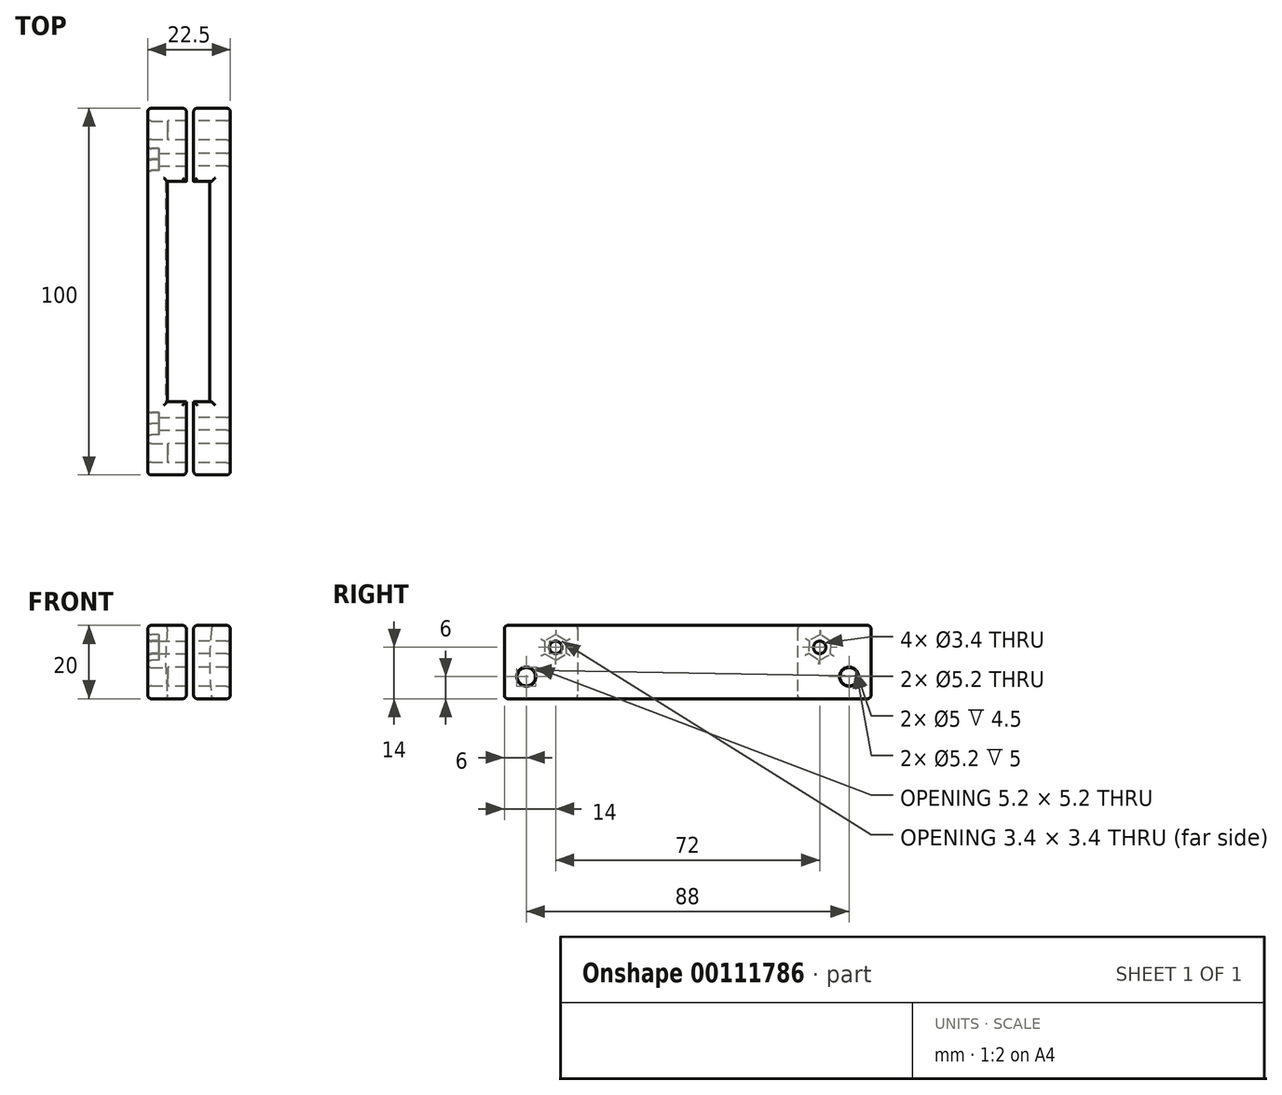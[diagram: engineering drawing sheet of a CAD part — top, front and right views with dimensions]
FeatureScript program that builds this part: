
annotation { "Feature Type Name" : "Feature", "Feature Type Description" : "" }
export const myFeature = defineFeature(function(context is Context, id is Id, definition is map)
    precondition{}
    {
        {
            var Q0;
            Q0=qCreatedBy(makeId("Top.planeOp"),FACE);
            var sketch = newSketch(context, id + "F0", { "sketchPlane" : qUnion([Q0])});
            skLineSegment(sketch, "E0.bottom", {"start": v(0, 0) * mm, "end": v(-5, 0) * mm});
            skLineSegment(sketch, "E0.top", {"start": v(0, 60) * mm, "end": v(-5, 60) * mm});
            skLineSegment(sketch, "E0.left", {"start": v(0, 0) * mm, "end": v(0, 60) * mm});
            skLineSegment(sketch, "E0.right", {"start": v(-5, 0) * mm, "end": v(-5, 60) * mm});
            skSolve(sketch);
        }
        {
            var Q0;
            Q0=makeQuery(id+"F0.imprint","IMPRINT",FACE,{"disambiguationData":[TD([[makeQuery(id+"F0.imprint","IMPRINT",EDGE,{"derivedFrom":sQuery(id+"F0.wireOp",EDGE,"E0.bottom")}),-1.0]])]});
            extrude(context, id + "F1", {"entities" : qUnion([Q0]), "depth" : 20 * mm});
        }
        {
            var Q0;
            Q0=makeQuery(id+"F1.opExtrude","SWEPT_FACE",FACE,{"disambiguationData":[OSD([sQuery(id+"F0.wireOp",EDGE,"E0.bottom")])]});
            var sketch = newSketch(context, id + "F2", { "sketchPlane" : qUnion([Q0])});
            skArc(sketch, "E1", {"start": v(0, 20) * mm, "mid": v(-0.63, 10) * mm, "end": v(0, 0) * mm});
            skSolve(sketch);
        }
        {
            var Q0;
            Q0=makeQuery(id+"F2.imprint","IMPRINT",FACE,{"disambiguationData":[TD([[makeQuery(id+"F2.imprint","IMPRINT",EDGE,{"derivedFrom":sQuery(id+"F2.wireOp",EDGE,"E1")}),1.0]])]});
            extrude(context, id + "F3", {"entities" : qUnion([Q0]), "operationType" : NewBodyOperationType.REMOVE, "endBound" : BoundingType.THROUGH_ALL, "oppositeDirection" : true, "depth" : 25 * mm});
        }
        {
            var Q0;
            Q0=makeQuery(id+"F1.opExtrude","SWEPT_FACE",FACE,{"disambiguationData":[OSD([sQuery(id+"F0.wireOp",EDGE,"E0.bottom")])]});
            var sketch = newSketch(context, id + "F4", { "sketchPlane" : qUnion([Q0])});
            skLineSegment(sketch, "E2.bottom", {"start": v(-5, 20) * mm, "end": v(0, 20) * mm});
            skLineSegment(sketch, "E2.top", {"start": v(-5, 0) * mm, "end": v(0, 0) * mm});
            skLineSegment(sketch, "E2.left", {"start": v(-5, 20) * mm, "end": v(-5, 0) * mm});
            skLineSegment(sketch, "E2.right", {"start": v(0, 20) * mm, "end": v(0, 0) * mm});
            skSolve(sketch);
        }
        {
            var Q0;
            Q0=makeQuery(id+"F4.imprint","IMPRINT",FACE,{"disambiguationData":[TD([[makeQuery(id+"F4.imprint","IMPRINT",EDGE,{"derivedFrom":sQuery(id+"F4.wireOp",EDGE,"E2.right")}),-1.0]])]});
            var Q1;
            Q1=makeQuery(id+"F4.imprint","IMPRINT",FACE,{"disambiguationData":[TD([[makeQuery(id+"F4.imprint","IMPRINT",EDGE,{"derivedFrom":sQuery(id+"F4.wireOp",EDGE,"E2.bottom")}),1.0]])]});
            extrude(context, id + "F5", {"entities" : qUnion([Q0, Q1]), "operationType" : NewBodyOperationType.ADD, "depth" : 20 * mm});
        }
        {
            var Q0;
            Q0=makeQuery(id+"F1.opExtrude","SWEPT_FACE",FACE,{"disambiguationData":[OSD([sQuery(id+"F0.wireOp",EDGE,"E0.top")])]});
            var sketch = newSketch(context, id + "F6", { "sketchPlane" : qUnion([Q0])});
            skLineSegment(sketch, "E3.bottom", {"start": v(5, 20) * mm, "end": v(0, 20) * mm});
            skLineSegment(sketch, "E3.top", {"start": v(5, 0) * mm, "end": v(0, 0) * mm});
            skLineSegment(sketch, "E3.left", {"start": v(5, 20) * mm, "end": v(5, 0) * mm});
            skLineSegment(sketch, "E3.right", {"start": v(0, 20) * mm, "end": v(0, 0) * mm});
            skSolve(sketch);
        }
        {
            var Q0;
            Q0=makeQuery(id+"F6.imprint","IMPRINT",FACE,{"disambiguationData":[TD([[makeQuery(id+"F6.imprint","IMPRINT",EDGE,{"derivedFrom":sQuery(id+"F6.wireOp",EDGE,"E3.right")}),1.0]])]});
            var Q1;
            Q1=makeQuery(id+"F6.imprint","IMPRINT",FACE,{"disambiguationData":[TD([[makeQuery(id+"F6.imprint","IMPRINT",EDGE,{"derivedFrom":sQuery(id+"F6.wireOp",EDGE,"E3.bottom")}),-1.0]])]});
            extrude(context, id + "F7", {"entities" : qUnion([Q0, Q1]), "operationType" : NewBodyOperationType.ADD, "depth" : 20 * mm});
        }
        {
            var Q0;
            Q0=makeQuery(id+"F7.opExtrude","SWEPT_FACE",FACE,{"disambiguationData":[OSD([sQuery(id+"F6.wireOp",EDGE,"E3.right")])]});
            var sketch = newSketch(context, id + "F8", { "sketchPlane" : qUnion([Q0])});
            skPoint(sketch, "E4", {"position": v(66, 14) * mm});
            skPoint(sketch, "E5", {"position": v(74, 6) * mm});
            skLineSegment(sketch, "E6", {"start": v(30, 27.75) * mm, "end": v(30, -11.02) * mm, "construction": true});
            skPoint(sketch, "E7.MirrorP", {"position": v(-6, 14) * mm});
            skPoint(sketch, "E8.MirrorP", {"position": v(-14, 6) * mm});
            skSolve(sketch);
        }
        {
            var Q0;
            Q0=sQuery(id+"F8.wireOp",VERTEX,"E7.MirrorP");
            var Q1;
            Q1=sQuery(id+"F8.wireOp",VERTEX,"E4");
            var Q2;
            Q2=makeQuery(id+"F1.opExtrude","SWEPT_BODY",BODY,{"disambiguationData":[OSD([sQuery(id+"F0.wireOp",EDGE,"E0.bottom"),sQuery(id+"F0.wireOp",EDGE,"E0.top"),sQuery(id+"F0.wireOp",EDGE,"E0.left"),sQuery(id+"F0.wireOp",EDGE,"E0.right")])]});
            hole(context, id + "F9", {"style" : HoleStyle.SIMPLE, "endStyle" : HoleEndStyle.BLIND, "standardTappedOrClearance" : lookupTablePath({ "standard" : "ISO", "size" : "3.4", "type" : "Drilled" }), "standardBlindInLast" : lookupTablePath({ "standard" : "ISO", "size" : "3.4", "type" : "Drilled" }), "holeDiameter" : 3.4 * mm, "holeDepth" : 12 * mm, "locations" : qUnion([Q0, Q1]), "scope" : qUnion([Q2])});
        }
        {
            var Q0;
            Q0=sQuery(id+"F8.wireOp",VERTEX,"E8.MirrorP");
            var Q1;
            Q1=sQuery(id+"F8.wireOp",VERTEX,"E5");
            var Q2;
            Q2=makeQuery(id+"F1.opExtrude","SWEPT_BODY",BODY,{"disambiguationData":[OSD([sQuery(id+"F0.wireOp",EDGE,"E0.bottom"),sQuery(id+"F0.wireOp",EDGE,"E0.top"),sQuery(id+"F0.wireOp",EDGE,"E0.left"),sQuery(id+"F0.wireOp",EDGE,"E0.right")])]});
            hole(context, id + "F10", {"style" : HoleStyle.SIMPLE, "endStyle" : HoleEndStyle.BLIND, "standardTappedOrClearance" : lookupTablePath({ "standard" : "ISO", "size" : "5", "type" : "Drilled" }), "standardBlindInLast" : lookupTablePath({ "standard" : "ISO", "size" : "5", "type" : "Drilled" }), "holeDiameter" : 5 * mm, "holeDepth" : 12 * mm, "locations" : qUnion([Q0, Q1]), "scope" : qUnion([Q2])});
        }
        {
            var Q0;
            Q0=makeQuery(id+"F7.boolean.opBoolean","MERGE",FACE,{"derivedFrom":[makeQuery(id+"F5.boolean.opBoolean","MERGE",FACE,{"derivedFrom":[makeQuery(id+"F1.opExtrude","SWEPT_FACE",FACE,{"disambiguationData":[OSD([sQuery(id+"F0.wireOp",EDGE,"E0.right")])]}),makeQuery(id+"F5.opExtrude","SWEPT_FACE",FACE,{"disambiguationData":[OSD([sQuery(id+"F4.wireOp",EDGE,"E2.left")])]})]}),makeQuery(id+"F7.opExtrude","SWEPT_FACE",FACE,{"disambiguationData":[OSD([sQuery(id+"F6.wireOp",EDGE,"E3.left")])]})]});
            var sketch = newSketch(context, id + "F11", { "sketchPlane" : qUnion([Q0])});
            skCircle(sketch, "E9.cCircle", {"center": v(6, 14) * mm, "radius": 3 * mm, "construction": true});
            skLineSegment(sketch, "E9.0", {"start": v(5.98, 10.54) * mm, "end": v(3, 12.28) * mm});
            skLineSegment(sketch, "E9.1", {"start": v(3, 12.28) * mm, "end": v(3, 15.75) * mm});
            skLineSegment(sketch, "E9.2", {"start": v(3, 15.75) * mm, "end": v(6.02, 17.46) * mm});
            skLineSegment(sketch, "E9.3", {"start": v(6.02, 17.46) * mm, "end": v(9, 15.72) * mm});
            skLineSegment(sketch, "E9.4", {"start": v(9, 15.72) * mm, "end": v(9, 12.25) * mm});
            skLineSegment(sketch, "E9.5", {"start": v(9, 12.25) * mm, "end": v(5.98, 10.54) * mm});
            skPoint(sketch, "E9.0.midPoint", {"position": v(4.49, 11.4) * mm});
            skCircle(sketch, "E10.cCircle", {"center": v(-66, 14) * mm, "radius": 3 * mm, "construction": true});
            skLineSegment(sketch, "E10.0", {"start": v(-62.94, 12.38) * mm, "end": v(-65.87, 10.54) * mm});
            skLineSegment(sketch, "E10.1", {"start": v(-65.87, 10.54) * mm, "end": v(-68.93, 12.16) * mm});
            skLineSegment(sketch, "E10.2", {"start": v(-68.93, 12.16) * mm, "end": v(-69.06, 15.62) * mm});
            skLineSegment(sketch, "E10.3", {"start": v(-69.06, 15.62) * mm, "end": v(-66.13, 17.46) * mm});
            skLineSegment(sketch, "E10.4", {"start": v(-66.13, 17.46) * mm, "end": v(-63.07, 15.84) * mm});
            skLineSegment(sketch, "E10.5", {"start": v(-63.07, 15.84) * mm, "end": v(-62.94, 12.38) * mm});
            skPoint(sketch, "E10.0.midPoint", {"position": v(-64.4, 11.46) * mm});
            skSolve(sketch);
        }
        {
            var Q0;
            Q0=makeQuery(id+"F11.imprint","IMPRINT",FACE,{"disambiguationData":[TD([[makeQuery(id+"F11.imprint","IMPRINT",EDGE,{"derivedFrom":sQuery(id+"F11.wireOp",EDGE,"E9.0")}),-1.0]])]});
            var Q1;
            Q1=makeQuery(id+"F11.imprint","IMPRINT",FACE,{"disambiguationData":[TD([[makeQuery(id+"F11.imprint","IMPRINT",EDGE,{"derivedFrom":sQuery(id+"F11.wireOp",EDGE,"E10.0")}),-1.0]])]});
            extrude(context, id + "F12", {"entities" : qUnion([Q0, Q1]), "operationType" : NewBodyOperationType.REMOVE, "oppositeDirection" : true, "depth" : 2.5 * mm});
        }
        {
            var Q0;
            Q0=makeQuery(id+"F7.boolean.opBoolean","MERGE",FACE,{"derivedFrom":[makeQuery(id+"F5.boolean.opBoolean","MERGE",FACE,{"derivedFrom":[makeQuery(id+"F1.opExtrude","SWEPT_FACE",FACE,{"disambiguationData":[OSD([sQuery(id+"F0.wireOp",EDGE,"E0.right")])]}),makeQuery(id+"F5.opExtrude","SWEPT_FACE",FACE,{"disambiguationData":[OSD([sQuery(id+"F4.wireOp",EDGE,"E2.left")])]})]}),makeQuery(id+"F7.opExtrude","SWEPT_FACE",FACE,{"disambiguationData":[OSD([sQuery(id+"F6.wireOp",EDGE,"E3.left")])]})]});
            extrude(context, id + "F13", {"entities" : qUnion([Q0]), "operationType" : NewBodyOperationType.ADD, "depth" : 0.5 * mm});
        }
        {
            var Q0;
            Q0=qCreatedBy(makeId("Top.planeOp"),FACE);
            var sketch = newSketch(context, id + "F14", { "sketchPlane" : qUnion([Q0])});
            skLineSegment(sketch, "E11.bottom", {"start": v(12, 0) * mm, "end": v(17, 0) * mm});
            skLineSegment(sketch, "E11.top", {"start": v(12, 60) * mm, "end": v(17, 60) * mm});
            skLineSegment(sketch, "E11.left", {"start": v(12, 0) * mm, "end": v(12, 60) * mm});
            skLineSegment(sketch, "E11.right", {"start": v(17, 0) * mm, "end": v(17, 60) * mm});
            skSolve(sketch);
        }
        {
            var Q0;
            Q0=makeQuery(id+"F14.imprint","IMPRINT",FACE,{"disambiguationData":[TD([[makeQuery(id+"F14.imprint","IMPRINT",EDGE,{"derivedFrom":sQuery(id+"F14.wireOp",EDGE,"E11.bottom")}),1.0]])]});
            extrude(context, id + "F15", {"entities" : qUnion([Q0]), "depth" : 20 * mm});
        }
        {
            var Q0;
            Q0=makeQuery(id+"F15.opExtrude","SWEPT_FACE",FACE,{"disambiguationData":[OSD([sQuery(id+"F14.wireOp",EDGE,"E11.bottom")])]});
            var sketch = newSketch(context, id + "F16", { "sketchPlane" : qUnion([Q0])});
            skArc(sketch, "E12", {"start": v(12, 20) * mm, "mid": v(11.37, 10) * mm, "end": v(12, 0) * mm});
            skSolve(sketch);
        }
        {
            var Q0;
            Q0=makeQuery(id+"F16.imprint","IMPRINT",FACE,{"disambiguationData":[TD([[makeQuery(id+"F16.imprint","IMPRINT",EDGE,{"derivedFrom":sQuery(id+"F16.wireOp",EDGE,"E12")}),1.0]])]});
            extrude(context, id + "F17", {"entities" : qUnion([Q0]), "operationType" : NewBodyOperationType.ADD, "oppositeDirection" : true, "depth" : 60 * mm});
        }
        {
            var Q0;
            {var subQ0=sQuery(id+"F14.wireOp",EDGE,"E11.bottom");Q0=makeQuery(id+"F17.boolean.opBoolean","MERGE",FACE,{"derivedFrom":[makeQuery(id+"F15.opExtrude","SWEPT_FACE",FACE,{"disambiguationData":[OSD([subQ0])]}),makeQuery(id+"F17.opExtrude","CAP_FACE",FACE,{"disambiguationData":[OSD([subQ0,sQuery(id+"F14.wireOp",EDGE,"E11.left"),sQuery(id+"F16.wireOp",EDGE,"E12")])],"isStart":true})]});}
            var sketch = newSketch(context, id + "F18", { "sketchPlane" : qUnion([Q0])});
            skLineSegment(sketch, "E13.bottom", {"start": v(17, 20) * mm, "end": v(12, 20) * mm});
            skLineSegment(sketch, "E13.top", {"start": v(17, 0) * mm, "end": v(12, 0) * mm});
            skLineSegment(sketch, "E13.left", {"start": v(17, 20) * mm, "end": v(17, 0) * mm});
            skLineSegment(sketch, "E13.right", {"start": v(12, 20) * mm, "end": v(12, 0) * mm});
            skSolve(sketch);
        }
        {
            var Q0;
            Q0=makeQuery(id+"F18.imprint","IMPRINT",FACE,{"disambiguationData":[TD([[makeQuery(id+"F18.imprint","IMPRINT",EDGE,{"derivedFrom":sQuery(id+"F18.wireOp",EDGE,"E13.bottom")}),-1.0]])]});
            extrude(context, id + "F19", {"entities" : qUnion([Q0]), "operationType" : NewBodyOperationType.ADD, "depth" : 20 * mm});
        }
        {
            var Q0;
            Q0=makeQuery(id+"F17.boolean.opBoolean","MERGE",FACE,{"derivedFrom":[makeQuery(id+"F15.opExtrude","SWEPT_FACE",FACE,{"disambiguationData":[OSD([sQuery(id+"F14.wireOp",EDGE,"E11.top")])]}),makeQuery(id+"F17.opExtrude","CAP_FACE",FACE,{"disambiguationData":[OSD([sQuery(id+"F14.wireOp",EDGE,"E11.bottom"),sQuery(id+"F14.wireOp",EDGE,"E11.left"),sQuery(id+"F16.wireOp",EDGE,"E12")])],"isStart":false})]});
            var sketch = newSketch(context, id + "F20", { "sketchPlane" : qUnion([Q0])});
            skLineSegment(sketch, "E14.bottom", {"start": v(-12, 20) * mm, "end": v(-17, 20) * mm});
            skLineSegment(sketch, "E14.top", {"start": v(-12, 0) * mm, "end": v(-17, 0) * mm});
            skLineSegment(sketch, "E14.left", {"start": v(-12, 20) * mm, "end": v(-12, 0) * mm});
            skLineSegment(sketch, "E14.right", {"start": v(-17, 20) * mm, "end": v(-17, 0) * mm});
            skSolve(sketch);
        }
        {
            var Q0;
            Q0=makeQuery(id+"F20.imprint","IMPRINT",FACE,{"disambiguationData":[TD([[makeQuery(id+"F20.imprint","IMPRINT",EDGE,{"derivedFrom":sQuery(id+"F20.wireOp",EDGE,"E14.bottom")}),1.0]])]});
            extrude(context, id + "F21", {"entities" : qUnion([Q0]), "operationType" : NewBodyOperationType.ADD, "depth" : 20 * mm});
        }
        {
            var Q0;
            {var subQ0=sQuery(id+"F6.wireOp",EDGE,"E3.right");Q0=makeQuery(id+"F8.imprint","IMPRINT",FACE,{"disambiguationData":[TD([[makeQuery(id+"F8.imprint","IMPRINT",EDGE,{"derivedFrom":makeQuery(id+"F7.opExtrude","CAP_EDGE",EDGE,{"disambiguationData":[OSD([subQ0])],"isStart":true})}),1.0]])]});}
            var Q1;
            Q1=makeQuery(id+"F5.opExtrude","SWEPT_FACE",FACE,{"disambiguationData":[OSD([sQuery(id+"F4.wireOp",EDGE,"E2.right")])]});
            extrude(context, id + "F22", {"entities" : qUnion([Q0, Q1]), "operationType" : NewBodyOperationType.ADD, "depth" : 5 * mm});
        }
        {
            var Q0;
            Q0=makeQuery(id+"F19.opExtrude","SWEPT_FACE",FACE,{"disambiguationData":[OSD([sQuery(id+"F18.wireOp",EDGE,"E13.right")])]});
            var Q1;
            Q1=makeQuery(id+"F21.opExtrude","SWEPT_FACE",FACE,{"disambiguationData":[OSD([sQuery(id+"F20.wireOp",EDGE,"E14.left")])]});
            extrude(context, id + "F23", {"entities" : qUnion([Q0, Q1]), "operationType" : NewBodyOperationType.ADD, "depth" : 5 * mm});
        }
        {
            var Q0;
            Q0=sQuery(id+"F8.wireOp",VERTEX,"E4");
            var Q1;
            Q1=sQuery(id+"F8.wireOp",VERTEX,"E7.MirrorP");
            var Q2;
            Q2=makeQuery(id+"F1.opExtrude","SWEPT_BODY",BODY,{"disambiguationData":[OSD([sQuery(id+"F0.wireOp",EDGE,"E0.bottom"),sQuery(id+"F0.wireOp",EDGE,"E0.top"),sQuery(id+"F0.wireOp",EDGE,"E0.left"),sQuery(id+"F0.wireOp",EDGE,"E0.right")])]});
            var Q3;
            Q3=makeQuery(id+"F15.opExtrude","SWEPT_BODY",BODY,{"disambiguationData":[OSD([sQuery(id+"F14.wireOp",EDGE,"E11.bottom"),sQuery(id+"F14.wireOp",EDGE,"E11.top"),sQuery(id+"F14.wireOp",EDGE,"E11.left"),sQuery(id+"F14.wireOp",EDGE,"E11.right")])]});
            hole(context, id + "F24", {"style" : HoleStyle.SIMPLE, "endStyle" : HoleEndStyle.BLIND, "oppositeDirection" : true, "holeDiameter" : 3.4 * mm, "holeDepth" : 50 * mm, "locations" : qUnion([Q0, Q1]), "scope" : qUnion([Q2, Q3])});
        }
        {
            var Q0;
            Q0=sQuery(id+"F8.wireOp",VERTEX,"E8.MirrorP");
            var Q1;
            Q1=sQuery(id+"F8.wireOp",VERTEX,"E5");
            var Q2;
            Q2=makeQuery(id+"F15.opExtrude","SWEPT_BODY",BODY,{"disambiguationData":[OSD([sQuery(id+"F14.wireOp",EDGE,"E11.bottom"),sQuery(id+"F14.wireOp",EDGE,"E11.top"),sQuery(id+"F14.wireOp",EDGE,"E11.left"),sQuery(id+"F14.wireOp",EDGE,"E11.right")])]});
            var Q3;
            Q3=makeQuery(id+"F1.opExtrude","SWEPT_BODY",BODY,{"disambiguationData":[OSD([sQuery(id+"F0.wireOp",EDGE,"E0.bottom"),sQuery(id+"F0.wireOp",EDGE,"E0.top"),sQuery(id+"F0.wireOp",EDGE,"E0.left"),sQuery(id+"F0.wireOp",EDGE,"E0.right")])]});
            hole(context, id + "F25", {"style" : HoleStyle.SIMPLE, "endStyle" : HoleEndStyle.BLIND, "oppositeDirection" : true, "holeDiameter" : 5.2 * mm, "holeDepth" : 50 * mm, "locations" : qUnion([Q0, Q1]), "scope" : qUnion([Q2, Q3])});
        }
        {
            var Q0;
            Q0=makeQuery(id+"F13.opExtrude","CAP_FACE",FACE,{"disambiguationData":[OSD([sQuery(id+"F0.wireOp",EDGE,"E0.right"),sQuery(id+"F4.wireOp",EDGE,"E2.left"),sQuery(id+"F6.wireOp",EDGE,"E3.left")])],"isStart":false});
            var Q1;
            Q1=makeQuery(id+"F21.boolean.opBoolean","MERGE",FACE,{"derivedFrom":[makeQuery(id+"F19.boolean.opBoolean","MERGE",FACE,{"derivedFrom":[makeQuery(id+"F15.opExtrude","SWEPT_FACE",FACE,{"disambiguationData":[OSD([sQuery(id+"F14.wireOp",EDGE,"E11.right")])]}),makeQuery(id+"F19.opExtrude","SWEPT_FACE",FACE,{"disambiguationData":[OSD([sQuery(id+"F18.wireOp",EDGE,"E13.left")])]})]}),makeQuery(id+"F21.opExtrude","SWEPT_FACE",FACE,{"disambiguationData":[OSD([sQuery(id+"F20.wireOp",EDGE,"E14.right")])]})]});
            var Q2;
            {var subQ0=sQuery(id+"F20.wireOp",EDGE,"E14.left");Q2=makeQuery(id+"F23.boolean.opBoolean","MERGE",FACE,{"derivedFrom":[makeQuery(id+"F21.opExtrude","CAP_FACE",FACE,{"disambiguationData":[OSD([sQuery(id+"F20.wireOp",EDGE,"E14.bottom"),sQuery(id+"F20.wireOp",EDGE,"E14.top"),subQ0,sQuery(id+"F20.wireOp",EDGE,"E14.right")])],"isStart":false}),makeQuery(id+"F23.opExtrude","SWEPT_FACE",FACE,{"disambiguationData":[OSD([subQ0]),TDD([makeQuery(id+"F21.opExtrude","CAP_EDGE",EDGE,{"disambiguationData":[OSD([subQ0])],"isStart":false})])]})]});}
            var Q3;
            {var subQ0=sQuery(id+"F6.wireOp",EDGE,"E3.right");var subQ1=sQuery(id+"F6.wireOp",EDGE,"E3.left");Q3=makeQuery(id+"F22.boolean.opBoolean","MERGE",FACE,{"derivedFrom":[makeQuery(id+"F13.boolean.opBoolean","MERGE",FACE,{"derivedFrom":[makeQuery(id+"F7.opExtrude","CAP_FACE",FACE,{"disambiguationData":[OSD([sQuery(id+"F6.wireOp",EDGE,"E3.bottom"),sQuery(id+"F6.wireOp",EDGE,"E3.top"),subQ1,subQ0])],"isStart":false}),makeQuery(id+"F13.opExtrude","SWEPT_FACE",FACE,{"disambiguationData":[OSD([subQ1])]})]}),makeQuery(id+"F22.opExtrude","SWEPT_FACE",FACE,{"disambiguationData":[OSD([subQ0]),TDD([makeQuery(id+"F8.imprint","IMPRINT",EDGE,{"derivedFrom":makeQuery(id+"F7.opExtrude","CAP_EDGE",EDGE,{"disambiguationData":[OSD([subQ0])],"isStart":false})})])]})]});}
            var Q4;
            {var subQ0=sQuery(id+"F20.wireOp",EDGE,"E14.bottom");var subQ1=sQuery(id+"F16.wireOp",EDGE,"E12");var subQ2=sQuery(id+"F18.wireOp",EDGE,"E13.bottom");Q4=makeQuery(id+"F23.boolean.opBoolean","MERGE",FACE,{"derivedFrom":[makeQuery(id+"F21.boolean.opBoolean","MERGE",FACE,{"derivedFrom":[makeQuery(id+"F19.boolean.opBoolean","MERGE",FACE,{"derivedFrom":[makeQuery(id+"F15.opExtrude","CAP_FACE",FACE,{"disambiguationData":[OSD([sQuery(id+"F14.wireOp",EDGE,"E11.bottom"),sQuery(id+"F14.wireOp",EDGE,"E11.top"),sQuery(id+"F14.wireOp",EDGE,"E11.left"),sQuery(id+"F14.wireOp",EDGE,"E11.right")])],"isStart":false}),makeQuery(id+"F19.opExtrude","SWEPT_FACE",FACE,{"disambiguationData":[OSD([subQ2])]})]}),makeQuery(id+"F21.opExtrude","SWEPT_FACE",FACE,{"disambiguationData":[OSD([subQ0])]})]}),makeQuery(id+"F23.opExtrude","SWEPT_FACE",FACE,{"disambiguationData":[OSD([subQ1,subQ2,sQuery(id+"F18.wireOp",EDGE,"E13.right")])]}),makeQuery(id+"F23.opExtrude","SWEPT_FACE",FACE,{"disambiguationData":[OSD([subQ1,subQ0,sQuery(id+"F20.wireOp",EDGE,"E14.left")])]})]});}
            var Q5;
            {var subQ0=sQuery(id+"F6.wireOp",EDGE,"E3.bottom");var subQ1=sQuery(id+"F2.wireOp",EDGE,"E1");var subQ2=sQuery(id+"F0.wireOp",EDGE,"E0.top");var subQ3=sQuery(id+"F4.wireOp",EDGE,"E2.bottom");var subQ4=sQuery(id+"F0.wireOp",EDGE,"E0.right");Q5=makeQuery(id+"F22.boolean.opBoolean","MERGE",FACE,{"derivedFrom":[makeQuery(id+"F13.boolean.opBoolean","MERGE",FACE,{"derivedFrom":[makeQuery(id+"F7.boolean.opBoolean","MERGE",FACE,{"derivedFrom":[makeQuery(id+"F5.boolean.opBoolean","MERGE",FACE,{"derivedFrom":[makeQuery(id+"F1.opExtrude","CAP_FACE",FACE,{"disambiguationData":[OSD([sQuery(id+"F0.wireOp",EDGE,"E0.bottom"),subQ2,sQuery(id+"F0.wireOp",EDGE,"E0.left"),subQ4])],"isStart":false}),makeQuery(id+"F5.opExtrude","SWEPT_FACE",FACE,{"disambiguationData":[OSD([subQ3])]})]}),makeQuery(id+"F7.opExtrude","SWEPT_FACE",FACE,{"disambiguationData":[OSD([subQ0])]})]}),makeQuery(id+"F13.opExtrude","SWEPT_FACE",FACE,{"disambiguationData":[OSD([subQ4,subQ3,sQuery(id+"F4.wireOp",EDGE,"E2.left"),subQ0,sQuery(id+"F6.wireOp",EDGE,"E3.left")])]})]}),makeQuery(id+"F22.opExtrude","SWEPT_FACE",FACE,{"disambiguationData":[OSD([subQ1,subQ3,sQuery(id+"F4.wireOp",EDGE,"E2.right")])]}),makeQuery(id+"F22.opExtrude","SWEPT_FACE",FACE,{"disambiguationData":[OSD([subQ2,subQ1,subQ0,sQuery(id+"F6.wireOp",EDGE,"E3.right")])]})]});}
            var Q6;
            {var subQ0=sQuery(id+"F18.wireOp",EDGE,"E13.right");Q6=makeQuery(id+"F23.boolean.opBoolean","MERGE",FACE,{"derivedFrom":[makeQuery(id+"F19.opExtrude","CAP_FACE",FACE,{"disambiguationData":[OSD([sQuery(id+"F18.wireOp",EDGE,"E13.bottom"),sQuery(id+"F18.wireOp",EDGE,"E13.top"),sQuery(id+"F18.wireOp",EDGE,"E13.left"),subQ0])],"isStart":false}),makeQuery(id+"F23.opExtrude","SWEPT_FACE",FACE,{"disambiguationData":[OSD([subQ0]),TDD([makeQuery(id+"F19.opExtrude","CAP_EDGE",EDGE,{"disambiguationData":[OSD([subQ0])],"isStart":false})])]})]});}
            var Q7;
            {var subQ0=sQuery(id+"F4.wireOp",EDGE,"E2.right");var subQ1=sQuery(id+"F4.wireOp",EDGE,"E2.left");Q7=makeQuery(id+"F22.boolean.opBoolean","MERGE",FACE,{"derivedFrom":[makeQuery(id+"F13.boolean.opBoolean","MERGE",FACE,{"derivedFrom":[makeQuery(id+"F5.opExtrude","CAP_FACE",FACE,{"disambiguationData":[OSD([sQuery(id+"F4.wireOp",EDGE,"E2.bottom"),sQuery(id+"F4.wireOp",EDGE,"E2.top"),subQ1,subQ0])],"isStart":false}),makeQuery(id+"F13.opExtrude","SWEPT_FACE",FACE,{"disambiguationData":[OSD([subQ1])]})]}),makeQuery(id+"F22.opExtrude","SWEPT_FACE",FACE,{"disambiguationData":[OSD([subQ0]),TDD([makeQuery(id+"F5.opExtrude","CAP_EDGE",EDGE,{"disambiguationData":[OSD([subQ0])],"isStart":false})])]})]});}
            var Q8;
            {var subQ0=sQuery(id+"F20.wireOp",EDGE,"E14.top");var subQ1=sQuery(id+"F16.wireOp",EDGE,"E12");var subQ2=sQuery(id+"F18.wireOp",EDGE,"E13.top");Q8=makeQuery(id+"F23.boolean.opBoolean","MERGE",FACE,{"derivedFrom":[makeQuery(id+"F21.boolean.opBoolean","MERGE",FACE,{"derivedFrom":[makeQuery(id+"F19.boolean.opBoolean","MERGE",FACE,{"derivedFrom":[makeQuery(id+"F15.opExtrude","CAP_FACE",FACE,{"disambiguationData":[OSD([sQuery(id+"F14.wireOp",EDGE,"E11.bottom"),sQuery(id+"F14.wireOp",EDGE,"E11.top"),sQuery(id+"F14.wireOp",EDGE,"E11.left"),sQuery(id+"F14.wireOp",EDGE,"E11.right")])],"isStart":true}),makeQuery(id+"F19.opExtrude","SWEPT_FACE",FACE,{"disambiguationData":[OSD([subQ2])]})]}),makeQuery(id+"F21.opExtrude","SWEPT_FACE",FACE,{"disambiguationData":[OSD([subQ0])]})]}),makeQuery(id+"F23.opExtrude","SWEPT_FACE",FACE,{"disambiguationData":[OSD([subQ1,subQ2,sQuery(id+"F18.wireOp",EDGE,"E13.right")])]}),makeQuery(id+"F23.opExtrude","SWEPT_FACE",FACE,{"disambiguationData":[OSD([subQ1,subQ0,sQuery(id+"F20.wireOp",EDGE,"E14.left")])]})]});}
            var Q9;
            {var subQ0=sQuery(id+"F6.wireOp",EDGE,"E3.top");var subQ1=sQuery(id+"F2.wireOp",EDGE,"E1");var subQ2=sQuery(id+"F0.wireOp",EDGE,"E0.top");var subQ3=sQuery(id+"F4.wireOp",EDGE,"E2.top");var subQ4=sQuery(id+"F0.wireOp",EDGE,"E0.right");Q9=makeQuery(id+"F22.boolean.opBoolean","MERGE",FACE,{"derivedFrom":[makeQuery(id+"F13.boolean.opBoolean","MERGE",FACE,{"derivedFrom":[makeQuery(id+"F7.boolean.opBoolean","MERGE",FACE,{"derivedFrom":[makeQuery(id+"F5.boolean.opBoolean","MERGE",FACE,{"derivedFrom":[makeQuery(id+"F1.opExtrude","CAP_FACE",FACE,{"disambiguationData":[OSD([sQuery(id+"F0.wireOp",EDGE,"E0.bottom"),subQ2,sQuery(id+"F0.wireOp",EDGE,"E0.left"),subQ4])],"isStart":true}),makeQuery(id+"F5.opExtrude","SWEPT_FACE",FACE,{"disambiguationData":[OSD([subQ3])]})]}),makeQuery(id+"F7.opExtrude","SWEPT_FACE",FACE,{"disambiguationData":[OSD([subQ0])]})]}),makeQuery(id+"F13.opExtrude","SWEPT_FACE",FACE,{"disambiguationData":[OSD([subQ4,subQ3,sQuery(id+"F4.wireOp",EDGE,"E2.left"),subQ0,sQuery(id+"F6.wireOp",EDGE,"E3.left")])]})]}),makeQuery(id+"F22.opExtrude","SWEPT_FACE",FACE,{"disambiguationData":[OSD([subQ1,subQ3,sQuery(id+"F4.wireOp",EDGE,"E2.right")])]}),makeQuery(id+"F22.opExtrude","SWEPT_FACE",FACE,{"disambiguationData":[OSD([subQ2,subQ1,subQ0,sQuery(id+"F6.wireOp",EDGE,"E3.right")])]})]});}
            fillet(context, id + "F26", {"entities" : qUnion([Q0, Q1, Q2, Q3, Q4, Q5, Q6, Q7, Q8, Q9]), "radius" : 1 * mm, "tangentPropagation" : true, "allowEdgeOverflow" : false});
        }
    });
